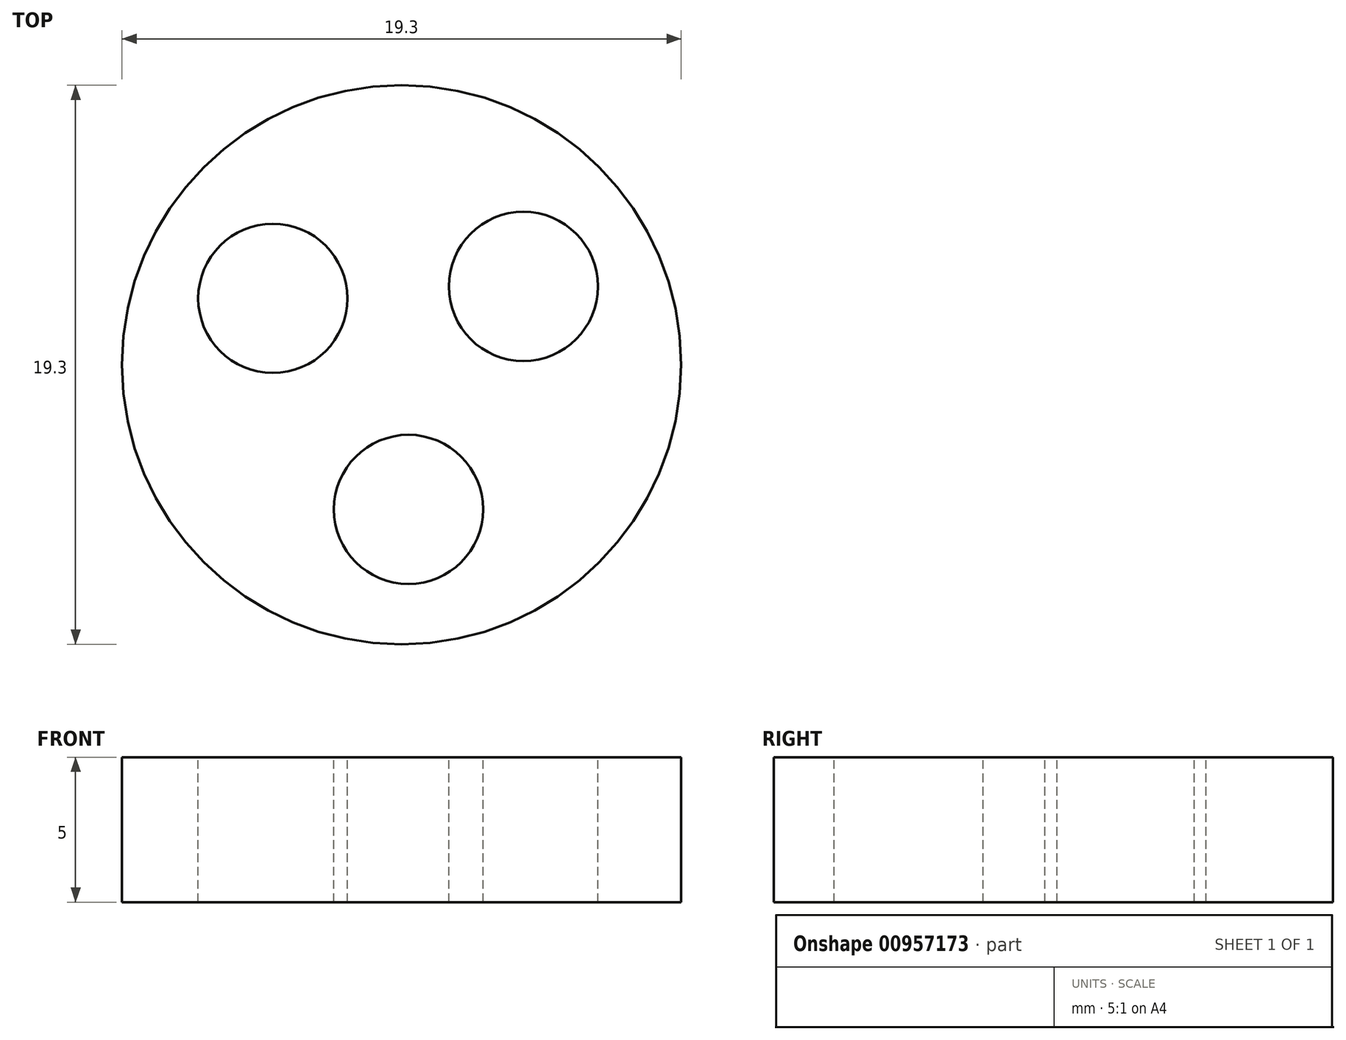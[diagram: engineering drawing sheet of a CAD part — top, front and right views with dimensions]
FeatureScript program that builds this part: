
annotation { "Feature Type Name" : "Feature", "Feature Type Description" : "" }
export const myFeature = defineFeature(function(context is Context, id is Id, definition is map)
    precondition{}
    {
        {
            var Q0;
            Q0=qCreatedBy(makeId("Top.planeOp"),FACE);
            var sketch = newSketch(context, id + "F0", { "sketchPlane" : qUnion([Q0])});
            skCircle(sketch, "E0", {"center": v(0, 0) * mm, "radius": 9.65 * mm});
            skSolve(sketch);
        }
        {
            var Q0;
            Q0 = qSketchRegion(id + "F0", true);
            extrude(context, id + "F1", {"entities" : qUnion([Q0]), "depth" : 5 * mm, "offsetDistance" : 25 * mm});
        }
        {
            var Q0;
            Q0=makeQuery(id+"F1.opExtrude","CAP_FACE",FACE,{"disambiguationData":[OSD([sQuery(id+"F0.wireOp",EDGE,"E0")])],"isStart":false});
            var sketch = newSketch(context, id + "F2", { "sketchPlane" : qUnion([Q0])});
            skCircle(sketch, "E1", {"center": v(0, 0) * mm, "radius": 5 * mm});
            skCircle(sketch, "E2", {"center": v(-4.44, 2.3) * mm, "radius": 2.58 * mm});
            skCircle(sketch, "E3.1.0", {"center": v(0.24, -5) * mm, "radius": 2.58 * mm});
            skCircle(sketch, "E3.2.0", {"center": v(4.2, 2.7) * mm, "radius": 2.58 * mm});
            skSolve(sketch);
        }
        {
            var Q0;
            {var subQ0=sQuery(id+"F2.wireOp",EDGE,"E3.2.0");var subQ1=sQuery(id+"F2.wireOp",EDGE,"E1");var subQ2=makeQuery(id+"F2.imprint","INTERSECT",VERTEX,{"disambiguationData":[OD(0.0)],"derivedFrom":[subQ1,subQ0]});Q0=makeQuery(id+"F2.imprint","IMPRINT",FACE,{"disambiguationData":[TD([[makeQuery(id+"F2.imprint","IMPRINT",EDGE,{"disambiguationData":[TD([[subQ2,1.0]])],"derivedFrom":subQ1}),1.0]])]});}
            var Q1;
            {var subQ0=sQuery(id+"F2.wireOp",EDGE,"E2");var subQ1=sQuery(id+"F2.wireOp",EDGE,"E1");var subQ2=makeQuery(id+"F2.imprint","INTERSECT",VERTEX,{"disambiguationData":[OD(0.0)],"derivedFrom":[subQ1,subQ0]});Q1=makeQuery(id+"F2.imprint","IMPRINT",FACE,{"disambiguationData":[TD([[makeQuery(id+"F2.imprint","IMPRINT",EDGE,{"disambiguationData":[TD([[subQ2,-1.0]])],"derivedFrom":subQ1}),-1.0]])]});}
            var Q2;
            {var subQ0=sQuery(id+"F2.wireOp",EDGE,"E2");var subQ1=sQuery(id+"F2.wireOp",EDGE,"E1");var subQ2=makeQuery(id+"F2.imprint","INTERSECT",VERTEX,{"disambiguationData":[OD(0.0)],"derivedFrom":[subQ1,subQ0]});Q2=makeQuery(id+"F2.imprint","IMPRINT",FACE,{"disambiguationData":[TD([[makeQuery(id+"F2.imprint","IMPRINT",EDGE,{"disambiguationData":[TD([[subQ2,-1.0]])],"derivedFrom":subQ1}),1.0]])]});}
            var Q3;
            {var subQ0=sQuery(id+"F2.wireOp",EDGE,"E3.1.0");var subQ1=sQuery(id+"F2.wireOp",EDGE,"E1");var subQ2=makeQuery(id+"F2.imprint","INTERSECT",VERTEX,{"disambiguationData":[OD(0.0)],"derivedFrom":[subQ1,subQ0]});Q3=makeQuery(id+"F2.imprint","IMPRINT",FACE,{"disambiguationData":[TD([[makeQuery(id+"F2.imprint","IMPRINT",EDGE,{"disambiguationData":[TD([[subQ2,-1.0]])],"derivedFrom":subQ1}),-1.0]])]});}
            var Q4;
            {var subQ0=sQuery(id+"F2.wireOp",EDGE,"E3.1.0");var subQ1=sQuery(id+"F2.wireOp",EDGE,"E1");var subQ2=makeQuery(id+"F2.imprint","INTERSECT",VERTEX,{"disambiguationData":[OD(0.0)],"derivedFrom":[subQ1,subQ0]});Q4=makeQuery(id+"F2.imprint","IMPRINT",FACE,{"disambiguationData":[TD([[makeQuery(id+"F2.imprint","IMPRINT",EDGE,{"disambiguationData":[TD([[subQ2,-1.0]])],"derivedFrom":subQ1}),1.0]])]});}
            var Q5;
            {var subQ0=sQuery(id+"F2.wireOp",EDGE,"E3.2.0");var subQ1=sQuery(id+"F2.wireOp",EDGE,"E1");var subQ2=makeQuery(id+"F2.imprint","INTERSECT",VERTEX,{"disambiguationData":[OD(0.0)],"derivedFrom":[subQ1,subQ0]});Q5=makeQuery(id+"F2.imprint","IMPRINT",FACE,{"disambiguationData":[TD([[makeQuery(id+"F2.imprint","IMPRINT",EDGE,{"disambiguationData":[TD([[subQ2,1.0]])],"derivedFrom":subQ1}),-1.0]])]});}
            extrude(context, id + "F3", {"entities" : qUnion([Q0, Q1, Q2, Q3, Q4, Q5]), "operationType" : NewBodyOperationType.REMOVE, "endBound" : BoundingType.THROUGH_ALL, "oppositeDirection" : true, "depth" : 25 * mm, "offsetDistance" : 25 * mm});
        }
    });
